# Revit family: Luna Deco 3 O - generic
name_source: partatom
category: Lighting Fixtures
units: mm (PartAtom-declared; Revit-internal decimal feet)

## family parameters
Base Level = No
Can host rebar = Yes
Construction Type = No
Dimming Lamp Color Temperature Shift = No
Fascia Depth = No
Name = 23.80.70.00
Ordinate Dimension Settings = Lighting
Subcategory = Normal
Thickness = No

## types (1)
- Luna Deco 3 0
    Alternate Units = Luna Deco 3 0
    Area = 0,01 m²
    Base Offset = https://www.sg-as.com
    Center of Gravity = X: 0,000 mm Y: -9,212 mm Z: 0,001 mm
    Density = 1000,00 kg/m³
    Design Status = 1
    Designer = she
    Is parametric = 0 mm  [stored 0 ft]
    Mass = 0,06 kg
    Material = Generic
    Model = Luna Deco 3 0
    Part Number = Luna Deco 3 O
    Preprocessor = SwSTEP 2.0
    Requested Accuracy = Low
    Revision Number = ANY
    Sending System = SolidWorks 2017
    Title = Luna Deco 3 O.STEP
    URL = Sg Armaturen
    Volume = 0,00 m³

note: [stored X ft] marks values corroborated as IEEE doubles in the binary element streams (Revit-internal decimal feet)

## geometry (parser evidence)
native form markers: Sweep x3
no freeform markers — native parametric forms only
